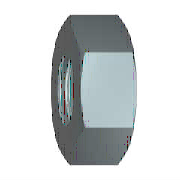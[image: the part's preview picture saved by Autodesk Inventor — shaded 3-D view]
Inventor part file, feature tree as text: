
AUTODESK INVENTOR PART (.ipt)
format: ipt  version: 2020 (Build 240168000, 168)  size: 163,840 bytes
history: native  units: mm (DEFAULTED — no unit token found)
features: sketch x3, other x2, extrude x1, hole x1, plane x1
ambient origin geometry x7: Origin, YZ Plane, XZ Plane, X Axis, Y Axis, Z Axis, Center Point
bodies: Solid1 (feature_tree)
feature tree (8):
  extrude  "Bryła"  Depth=6.350853mm
  other  "Faza1"
  hole  "Gwint"  [1 undecoded]
  other  "Work Axis1"
  plane  "Work Plane1"
  sketch  "Szkic1"
  sketch  "Szkic2"
  sketch  "Szkic3"
note: 1 required parameter value undecoded (feature->parameter linkage not recoverable at this tier; creation-order binding heuristic only, values carry confidence <= 0.55)
